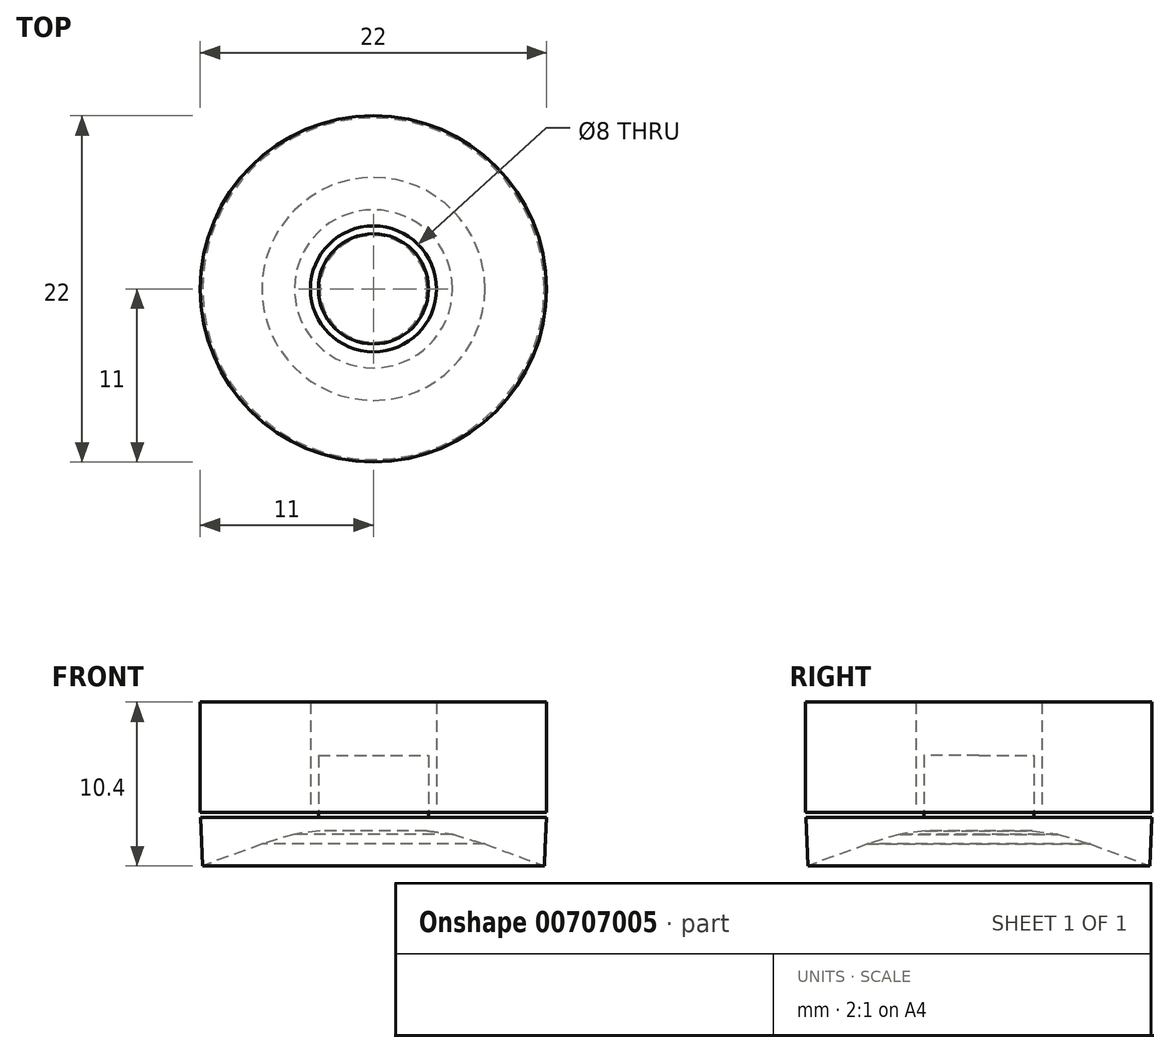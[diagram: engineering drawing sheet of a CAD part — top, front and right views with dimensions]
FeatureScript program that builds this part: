
annotation { "Feature Type Name" : "Feature", "Feature Type Description" : "" }
export const myFeature = defineFeature(function(context is Context, id is Id, definition is map)
    precondition{}
    {
        {
            var Q0;
            Q0=qCreatedBy(makeId("Top.planeOp"),FACE);
            var sketch = newSketch(context, id + "F0", { "sketchPlane" : qUnion([Q0])});
            skCircle(sketch, "E0", {"center": v(0, 0) * mm, "radius": 4 * mm});
            skCircle(sketch, "E1", {"center": v(0, 0) * mm, "radius": 11 * mm});
            skSolve(sketch);
        }
        {
            var Q0;
            Q0=makeQuery(id+"F0.imprint","IMPRINT",FACE,{"disambiguationData":[TD([[makeQuery(id+"F0.imprint","IMPRINT",EDGE,{"derivedFrom":sQuery(id+"F0.wireOp",EDGE,"E0")}),-1.0]])]});
            extrude(context, id + "F1", {"entities" : qUnion([Q0]), "depth" : 7 * mm, "offsetDistance" : 25 * mm});
        }
        {
            var Q0;
            Q0=qCreatedBy(makeId("Top.planeOp"),FACE);
            var sketch = newSketch(context, id + "F2", { "sketchPlane" : qUnion([Q0])});
            skCircle(sketch, "E2", {"center": v(0, 0) * mm, "radius": 40 * mm});
            skCircle(sketch, "E3", {"center": v(0, 0) * mm, "radius": 11.5 * mm});
            skSolve(sketch);
        }
        {
            var Q0;
            Q0=makeQuery(id+"F2.imprint","IMPRINT",FACE,{"disambiguationData":[TD([[makeQuery(id+"F2.imprint","IMPRINT",EDGE,{"derivedFrom":sQuery(id+"F2.wireOp",EDGE,"E2")}),1.0]])]});
            extrude(context, id + "F3", {"entities" : qUnion([Q0]), "depth" : 7 * mm, "offsetDistance" : 25 * mm});
        }
        {
            var Q0;
            Q0=makeQuery(id+"F3.opExtrude","CAP_FACE",FACE,{"disambiguationData":[OSD([sQuery(id+"F2.wireOp",EDGE,"E2"),sQuery(id+"F2.wireOp",EDGE,"E3")])],"isStart":false});
            var sketch = newSketch(context, id + "F4", { "sketchPlane" : qUnion([Q0])});
            skCircle(sketch, "E4", {"center": v(0, 26.65) * mm, "radius": 11.5 * mm});
            skSolve(sketch);
        }
        {
            var Q0;
            Q0 = qSketchRegion(id + "F4", true);
            extrude(context, id + "F5", {"entities" : qUnion([Q0]), "operationType" : NewBodyOperationType.REMOVE, "oppositeDirection" : true, "depth" : 25 * mm, "offsetDistance" : 25 * mm});
        }
        {
            var Q0;
            Q0=makeQuery(id+"F3.opExtrude","SWEPT_BODY",BODY,{"disambiguationData":[OSD([sQuery(id+"F2.wireOp",EDGE,"E2"),sQuery(id+"F2.wireOp",EDGE,"E3")])]});
            deleteBodies(context, id + "F6", {"entities" : qUnion([Q0])});
        }
        {
            var Q0;
            Q0=qCreatedBy(makeId("Top.planeOp"),FACE);
            var sketch = newSketch(context, id + "F7", { "sketchPlane" : qUnion([Q0])});
            skCircle(sketch, "E5", {"center": v(0, 0) * mm, "radius": 3.5 * mm});
            skSolve(sketch);
        }
        {
            var Q0;
            Q0=makeQuery(id+"F7.imprint","IMPRINT",FACE,{"disambiguationData":[TD([[makeQuery(id+"F7.imprint","IMPRINT",EDGE,{"derivedFrom":sQuery(id+"F7.wireOp",EDGE,"E5")}),1.0]])]});
            extrude(context, id + "F8", {"entities" : qUnion([Q0]), "depth" : 3.6 * mm, "offsetDistance" : 25 * mm});
        }
        {
            var Q0;
            Q0=qCreatedBy(makeId("Front.planeOp"),FACE);
            var sketch = newSketch(context, id + "F9", { "sketchPlane" : qUnion([Q0])});
            skLineSegment(sketch, "E6", {"start": v(10.93, -0.22) * mm, "end": v(10.93, -2.65) * mm});
            skLineSegment(sketch, "E7", {"start": v(0, 0) * mm, "end": v(0, -1.3) * mm});
            skLineSegment(sketch, "E8", {"start": v(10.93, -0.22) * mm, "end": v(0, 0) * mm});
            skLineSegment(sketch, "E9", {"start": v(10.93, -2.65) * mm, "end": v(10.18, -2.28) * mm});
            skLineSegment(sketch, "E10", {"start": v(10.18, -2.28) * mm, "end": v(9.03, -1.82) * mm});
            skLineSegment(sketch, "E11", {"start": v(9.03, -1.82) * mm, "end": v(7.26, -1.6) * mm});
            skLineSegment(sketch, "E12", {"start": v(7.26, -1.6) * mm, "end": v(3.7, -1.27) * mm});
            skLineSegment(sketch, "E13", {"start": v(3.7, -1.27) * mm, "end": v(0, -1.3) * mm});
            skSolve(sketch);
        }
        {
            var Q0;
            Q0 = qSketchRegion(id + "F9", true);
            var Q1;
            Q1=sQuery(id+"F9.wireOp",EDGE,"E7");
            revolve(context, id + "F10", {"surfaceOperationType" : NewSurfaceOperationType.NEW, "entities" : qUnion([Q0]), "axis" : qUnion([Q1]), "revolveType" : RevolveType.FULL});
        }
        {
            var Q0;
            Q0=makeQuery(id+"F8.opExtrude","CAP_FACE",FACE,{"disambiguationData":[OSD([sQuery(id+"F7.wireOp",EDGE,"E5")])],"isStart":false});
            extrude(context, id + "F11", {"entities" : qUnion([Q0]), "oppositeDirection" : true, "depth" : 4.8 * mm, "offsetDistance" : 25 * mm});
        }
        {
            var Q0;
            Q0=makeQuery(id+"F11.opExtrude","SWEPT_BODY",BODY,{"disambiguationData":[OSD([sQuery(id+"F7.wireOp",EDGE,"E5")])]});
            var Q1;
            Q1=makeQuery(id+"F10.opRevolve","SWEPT_BODY",BODY,{"disambiguationData":[OSD([sQuery(id+"F9.wireOp",EDGE,"E6"),sQuery(id+"F9.wireOp",EDGE,"E7"),sQuery(id+"F9.wireOp",EDGE,"E8"),sQuery(id+"F9.wireOp",EDGE,"E9"),sQuery(id+"F9.wireOp",EDGE,"E10"),sQuery(id+"F9.wireOp",EDGE,"E11"),sQuery(id+"F9.wireOp",EDGE,"E12"),sQuery(id+"F9.wireOp",EDGE,"E13")])]});
            deleteBodies(context, id + "F12", {"entities" : qUnion([Q0, Q1])});
        }
        {
            var Q0;
            Q0=makeQuery(id+"F8.opExtrude","CAP_FACE",FACE,{"disambiguationData":[OSD([sQuery(id+"F7.wireOp",EDGE,"E5")])],"isStart":true});
            extrude(context, id + "F13", {"entities" : qUnion([Q0]), "operationType" : NewBodyOperationType.ADD, "depth" : 1 * mm, "offsetDistance" : 25 * mm});
        }
        {
            var Q0;
            Q0=qCreatedBy(makeId("Front.planeOp"),FACE);
            var sketch = newSketch(context, id + "F14", { "sketchPlane" : qUnion([Q0])});
            skLineSegment(sketch, "E14", {"start": v(11, -0.31) * mm, "end": v(0, -0.31) * mm});
            skLineSegment(sketch, "E15", {"start": v(0, -0.31) * mm, "end": v(0, -1.17) * mm});
            skLineSegment(sketch, "E16", {"start": v(0, -1.17) * mm, "end": v(3.4, -1.17) * mm});
            skLineSegment(sketch, "E17", {"start": v(3.4, -1.17) * mm, "end": v(5.02, -1.39) * mm});
            skLineSegment(sketch, "E18", {"start": v(5.02, -1.39) * mm, "end": v(7.08, -2.02) * mm});
            skLineSegment(sketch, "E19", {"start": v(7.08, -2.02) * mm, "end": v(10.85, -3.4) * mm});
            skLineSegment(sketch, "E20", {"start": v(10.85, -3.4) * mm, "end": v(11, -0.31) * mm});
            skSolve(sketch);
        }
        {
            var Q0;
            Q0 = qSketchRegion(id + "F14", true);
            var Q1;
            Q1=sQuery(id+"F14.wireOp",EDGE,"E15");
            revolve(context, id + "F15", {"operationType" : NewBodyOperationType.ADD, "surfaceOperationType" : NewSurfaceOperationType.NEW, "entities" : qUnion([Q0]), "axis" : qUnion([Q1]), "revolveType" : RevolveType.FULL});
        }
    });
